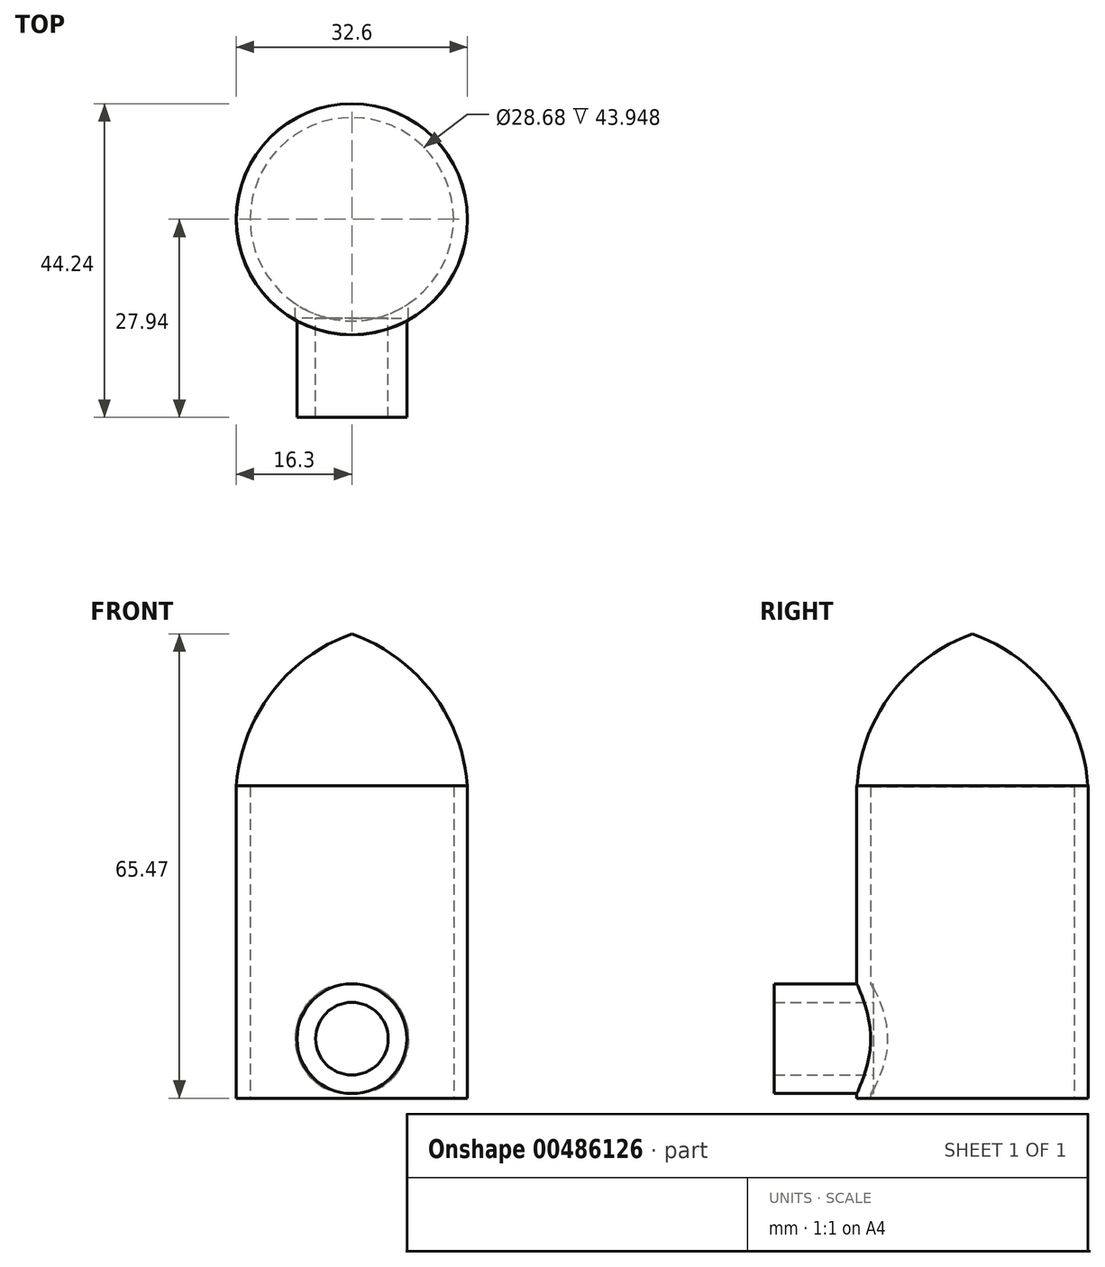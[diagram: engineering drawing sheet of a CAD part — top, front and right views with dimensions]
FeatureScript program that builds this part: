
annotation { "Feature Type Name" : "Feature", "Feature Type Description" : "" }
export const myFeature = defineFeature(function(context is Context, id is Id, definition is map)
    precondition{}
    {
        {
            var Q0;
            Q0=qCreatedBy(makeId("Top.planeOp"),FACE);
            var sketch = newSketch(context, id + "F0", { "sketchPlane" : qUnion([Q0])});
            skCircle(sketch, "E0", {"center": v(0, 0) * mm, "radius": 14.34 * mm});
            skCircle(sketch, "E1", {"center": v(0, 0) * mm, "radius": 16.3 * mm});
            skSolve(sketch);
        }
        {
            var Q0;
            Q0=qSketchRegion(id+"F0",true);
            extrude(context, id + "F1", {"entities" : qUnion([Q0]), "depth" : 44.07 * mm});
        }
        {
            var Q0;
            Q0=qCreatedBy(makeId("Front.planeOp"),FACE);
            var sketch = newSketch(context, id + "F2", { "sketchPlane" : qUnion([Q0])});
            skCircle(sketch, "E2", {"center": v(0, 8.38) * mm, "radius": 7.73 * mm});
            skSolve(sketch);
        }
        {
            var Q0;
            Q0=qSketchRegion(id+"F2",true);
            extrude(context, id + "F3", {"entities" : qUnion([Q0]), "operationType" : NewBodyOperationType.ADD, "depth" : 27.94 * mm});
        }
        {
            var Q0;
            Q0=makeQuery(id+"F3.opExtrude","CAP_FACE",FACE,{"disambiguationData":[OSD([sQuery(id+"F2.wireOp",EDGE,"E2")])],"isStart":true});
            var sketch = newSketch(context, id + "F4", { "sketchPlane" : qUnion([Q0])});
            skCircle(sketch, "E3", {"center": v(0, 8.38) * mm, "radius": 7.96 * mm});
            skSolve(sketch);
        }
        {
            var Q0;
            Q0=qSketchRegion(id+"F4",true);
            extrude(context, id + "F5", {"entities" : qUnion([Q0]), "operationType" : NewBodyOperationType.REMOVE, "oppositeDirection" : true, "depth" : 13.97 * mm});
        }
        {
            var Q0;
            Q0=makeQuery(id+"F5.boolean.opBoolean","COPY",FACE,{"derivedFrom":makeQuery(id+"F5.opExtrude","CAP_FACE",FACE,{"disambiguationData":[OSD([sQuery(id+"F4.wireOp",EDGE,"E3")])],"isStart":false})});
            var sketch = newSketch(context, id + "F6", { "sketchPlane" : qUnion([Q0])});
            skLineSegment(sketch, "E4.bottom", {"start": v(-5.08, 8.38) * mm, "end": v(5.08, 8.38) * mm});
            skLineSegment(sketch, "E4.top", {"start": v(-5.08, 8.38) * mm, "end": v(5.08, 8.38) * mm});
            skLineSegment(sketch, "E4.left", {"start": v(-5.08, 8.38) * mm, "end": v(-5.08, 8.38) * mm});
            skLineSegment(sketch, "E4.right", {"start": v(5.08, 8.38) * mm, "end": v(5.08, 8.38) * mm});
            skPoint(sketch, "E4.middle", {"position": v(0, 8.38) * mm});
            skCircle(sketch, "E5", {"center": v(0, 8.38) * mm, "radius": 5.11 * mm});
            skSolve(sketch);
        }
        {
            var Q0;
            Q0=qSketchRegion(id+"F6",true);
            extrude(context, id + "F7", {"entities" : qUnion([Q0]), "operationType" : NewBodyOperationType.REMOVE, "oppositeDirection" : true, "depth" : 25.4 * mm});
        }
        {
            var Q0;
            Q0=qCreatedBy(makeId("Right.planeOp"),FACE);
            var sketch = newSketch(context, id + "F8", { "sketchPlane" : qUnion([Q0])});
            skLineSegment(sketch, "E6", {"start": v(16.3, 43.95) * mm, "end": v(-16.28, 43.95) * mm});
            skLineSegment(sketch, "E7", {"start": v(0, 65.47) * mm, "end": v(0, 43.95) * mm});
            skArc(sketch, "E8", {"start": v(0, 65.47) * mm, "mid": v(-11.35, 57.14) * mm, "end": v(-16.28, 43.95) * mm});
            skSolve(sketch);
        }
        {
            var Q0;
            Q0=qSketchRegion(id+"F8",true);
            var Q1;
            Q1=sQuery(id+"F8.wireOp",EDGE,"E7");
            revolve(context, id + "F9", {"operationType" : NewBodyOperationType.ADD, "entities" : qUnion([Q0]), "axis" : qUnion([Q1]), "revolveType" : RevolveType.FULL});
        }
    });
